# Revit family: Haworth_CabanaLounge_ChaiseLounge
name_source: partatom
category: Furniture
revit_build: Autodesk Revit 2018 (Build: 20170223_1515(x64)
units: mm (PartAtom-declared; Revit-internal decimal feet)

## family parameters
Always vertical = Yes
Cut with Voids When Loaded = No
OmniClass Number = 23.40.70.14.64.21
OmniClass Title = Systems Furniture
Room Calculation Point = No
Shared = No
Work Plane-Based = No

## types (3) — shared parameters
Assembly Code = E2020200
Back Width = 30"
Leg Offset = 2 3/4"
Manufacturer = Haworth
Model = Haworth Cabana
Revision Number = 1
Screen Width = 32"
Seat Depth = 30"
Seat Height = 18 1/16"
Seat Width = 60"
Size = Verify Final Dim. w/ Haworth
URL = http://www.haworth.com
URL - Product = https://www.haworth.com
Warranty = http://www.haworth.com

## per-type parameters (varying)
| type | Actual Depth | Actual Height | Actual Width | Description | High Screen | Low Screen | No Screen | With Screen |
| S9DC-H - High Screen | 32" | 54" | 62" | Haworth Cabana Chaise Lounge - High Screen | Yes | No | No | Yes |
| S9DC-L - Low Screen | 32" | 42" | 62" | Haworth Cabana Chaise Lounge - Low Screen | No | Yes | No | Yes |
| S9DC-0 - No Screen | 30" | 30 3/8" | 60" | Haworth Cabana Chaise Lounge - No Screen | No | No | Yes | No |

## geometry (parser evidence)
native form markers: Extrusion x1, Sweep x11
no freeform markers — native parametric forms only
